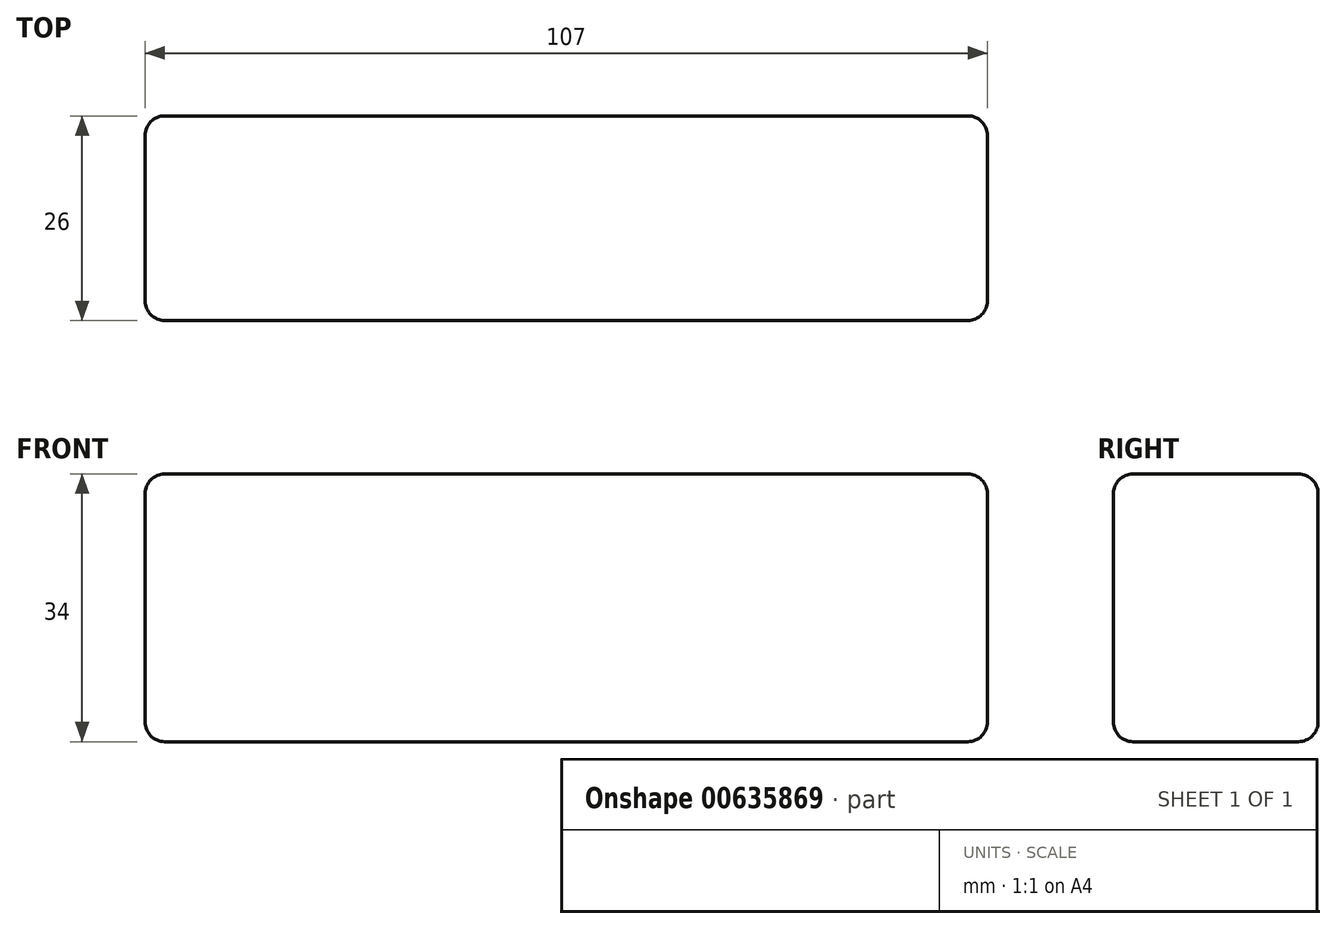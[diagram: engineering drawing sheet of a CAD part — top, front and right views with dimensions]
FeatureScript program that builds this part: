
annotation { "Feature Type Name" : "Feature", "Feature Type Description" : "" }
export const myFeature = defineFeature(function(context is Context, id is Id, definition is map)
    precondition{}
    {
        {
            var Q0;
            Q0=qCreatedBy(makeId("Top.planeOp"),FACE);
            var sketch = newSketch(context, id + "F0", { "sketchPlane" : qUnion([Q0])});
            skLineSegment(sketch, "E0.bottom", {"start": v(0, 0) * mm, "end": v(107, 0) * mm});
            skLineSegment(sketch, "E0.top", {"start": v(0, 26) * mm, "end": v(107, 26) * mm});
            skLineSegment(sketch, "E0.left", {"start": v(0, 0) * mm, "end": v(0, 26) * mm});
            skLineSegment(sketch, "E0.right", {"start": v(107, 0) * mm, "end": v(107, 26) * mm});
            skSolve(sketch);
        }
        {
            var Q0;
            Q0 = qSketchRegion(id + "F0", true);
            extrude(context, id + "F1", {"entities" : qUnion([Q0]), "depth" : 34 * mm, "offsetDistance" : 25 * mm});
        }
        {
            var Q0;
            Q0=makeQuery(id+"F1.opExtrude","SWEPT_FACE",FACE,{"disambiguationData":[OSD([sQuery(id+"F0.wireOp",EDGE,"E0.bottom")])]});
            var Q1;
            Q1=makeQuery(id+"F1.opExtrude","SWEPT_FACE",FACE,{"disambiguationData":[OSD([sQuery(id+"F0.wireOp",EDGE,"E0.top")])]});
            var Q2;
            Q2=makeQuery(id+"F1.opExtrude","SWEPT_FACE",FACE,{"disambiguationData":[OSD([sQuery(id+"F0.wireOp",EDGE,"E0.left")])]});
            var Q3;
            Q3=makeQuery(id+"F1.opExtrude","CAP_FACE",FACE,{"disambiguationData":[OSD([sQuery(id+"F0.wireOp",EDGE,"E0.bottom"),sQuery(id+"F0.wireOp",EDGE,"E0.top"),sQuery(id+"F0.wireOp",EDGE,"E0.left"),sQuery(id+"F0.wireOp",EDGE,"E0.right")])],"isStart":false});
            var Q4;
            Q4=makeQuery(id+"F1.opExtrude","SWEPT_FACE",FACE,{"disambiguationData":[OSD([sQuery(id+"F0.wireOp",EDGE,"E0.right")])]});
            var Q5;
            Q5=makeQuery(id+"F1.opExtrude","CAP_FACE",FACE,{"disambiguationData":[OSD([sQuery(id+"F0.wireOp",EDGE,"E0.bottom"),sQuery(id+"F0.wireOp",EDGE,"E0.top"),sQuery(id+"F0.wireOp",EDGE,"E0.left"),sQuery(id+"F0.wireOp",EDGE,"E0.right")])],"isStart":true});
            fillet(context, id + "F2", {"entities" : qUnion([Q0, Q1, Q2, Q3, Q4, Q5]), "radius" : 2.5 * mm, "tangentPropagation" : true, "allowEdgeOverflow" : false});
        }
    });
